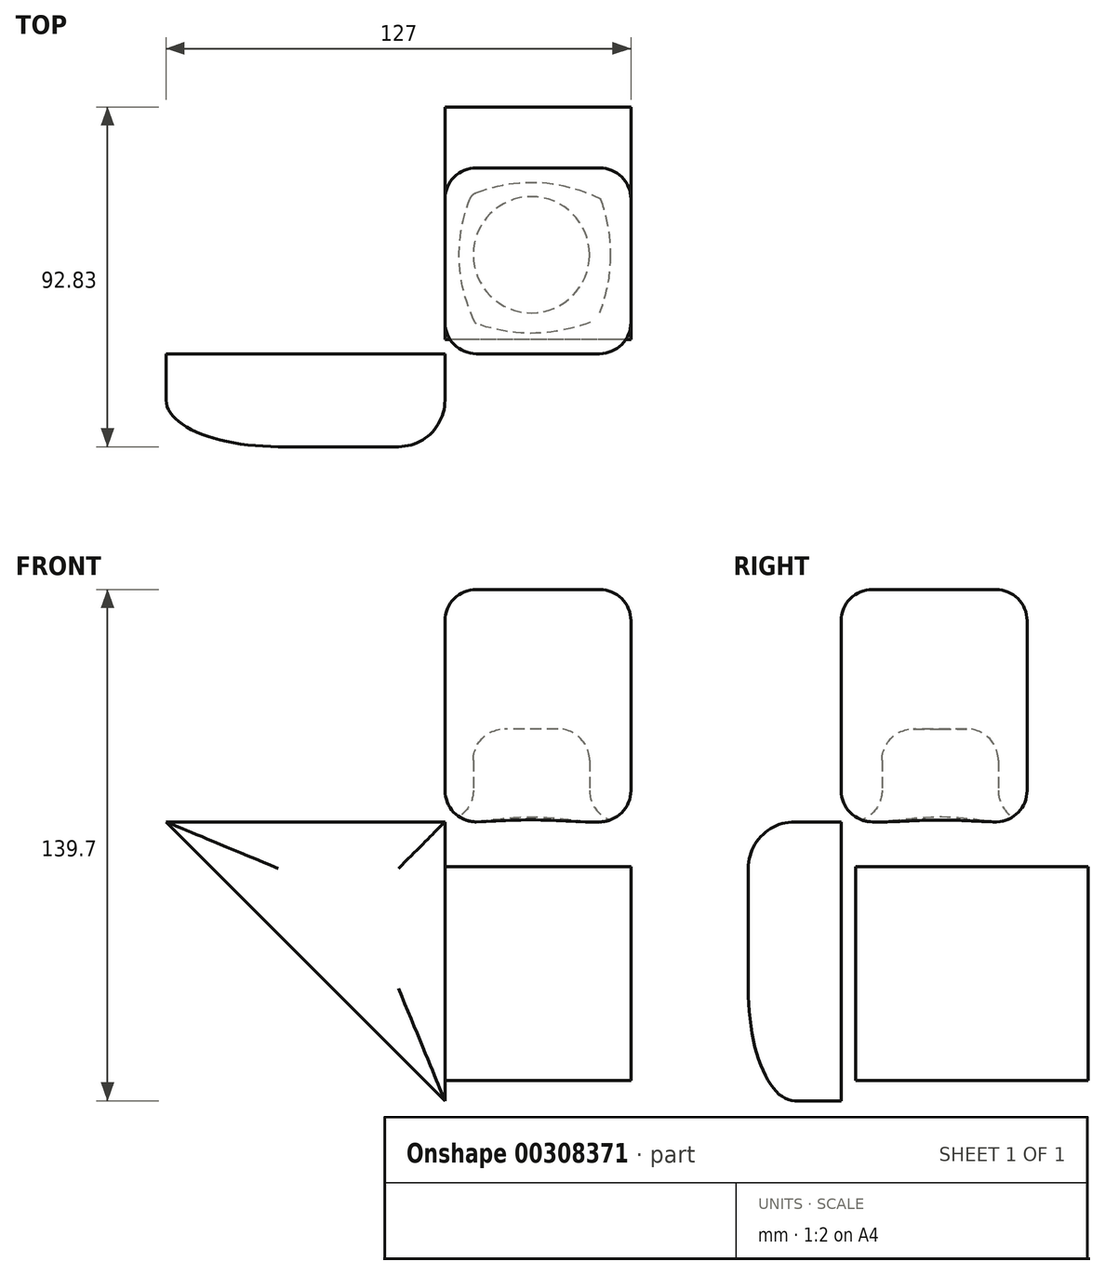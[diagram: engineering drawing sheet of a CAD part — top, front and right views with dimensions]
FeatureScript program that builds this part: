
annotation { "Feature Type Name" : "Feature", "Feature Type Description" : "" }
export const myFeature = defineFeature(function(context is Context, id is Id, definition is map)
    precondition{}
    {
        {
            var Q0;
            Q0=qCreatedBy(makeId("Top.planeOp"),FACE);
            var sketch = newSketch(context, id + "F0", { "sketchPlane" : qUnion([Q0])});
            skLineSegment(sketch, "E0", {"start": v(0, 0) * mm, "end": v(50.8, 0) * mm});
            skLineSegment(sketch, "E1", {"start": v(0, 0) * mm, "end": v(0, 50.8) * mm});
            skLineSegment(sketch, "E2", {"start": v(0, 50.8) * mm, "end": v(50.8, 50.8) * mm});
            skLineSegment(sketch, "E3", {"start": v(50.8, 50.8) * mm, "end": v(50.8, 0) * mm});
            skSolve(sketch);
        }
        {
            var Q0;
            Q0 = qSketchRegion(id + "F0", true);
            extrude(context, id + "F1", {"entities" : qUnion([Q0]), "depth" : 63.5 * mm});
        }
        {
            var Q0;
            Q0=qCreatedBy(makeId("Top.planeOp"),FACE);
            var sketch = newSketch(context, id + "F2", { "sketchPlane" : qUnion([Q0])});
            skCircle(sketch, "E4", {"center": v(23.6, 27.04) * mm, "radius": 15.88 * mm});
            skSolve(sketch);
        }
        {
            var Q0;
            Q0=makeQuery(id+"F2.imprint","IMPRINT",FACE,{"disambiguationData":[TD([[makeQuery(id+"F2.imprint","IMPRINT",EDGE,{"derivedFrom":sQuery(id+"F2.wireOp",EDGE,"E4")}),1.0]])]});
            var Q1;
            Q1=sQuery(id+"F2.wireOp",EDGE,"E4");
            extrude(context, id + "F3", {"entities" : qUnion([Q0]), "surfaceEntities" : qUnion([Q1]), "depth" : 25.4 * mm});
        }
        {
            var Q0;
            Q0=makeQuery(id+"F3.opExtrude","SWEPT_BODY",BODY,{"disambiguationData":[OSD([sQuery(id+"F2.wireOp",EDGE,"E4")])]});
            var Q1;
            Q1=makeQuery(id+"F1.opExtrude","SWEPT_BODY",BODY,{"disambiguationData":[OSD([sQuery(id+"F0.wireOp",EDGE,"E0"),sQuery(id+"F0.wireOp",EDGE,"E1"),sQuery(id+"F0.wireOp",EDGE,"E2"),sQuery(id+"F0.wireOp",EDGE,"E3")])]});
            booleanBodies(context, id + "F4", {"operationType" : BooleanOperationType.SUBTRACTION, "tools" : qUnion([Q0]), "targets" : qUnion([Q1])});
        }
        {
            var Q0;
            Q0=makeQuery(id+"F1.opExtrude","SWEPT_FACE",FACE,{"disambiguationData":[OSD([sQuery(id+"F0.wireOp",EDGE,"E1")])]});
            var Q1;
            Q1=makeQuery(id+"F1.opExtrude","SWEPT_FACE",FACE,{"disambiguationData":[OSD([sQuery(id+"F0.wireOp",EDGE,"E2")])]});
            var Q2;
            Q2=makeQuery(id+"F1.opExtrude","SWEPT_FACE",FACE,{"disambiguationData":[OSD([sQuery(id+"F0.wireOp",EDGE,"E0")])]});
            var Q3;
            Q3=makeQuery(id+"F1.opExtrude","SWEPT_FACE",FACE,{"disambiguationData":[OSD([sQuery(id+"F0.wireOp",EDGE,"E3")])]});
            var Q4;
            Q4=makeQuery(id+"F1.opExtrude","CAP_FACE",FACE,{"disambiguationData":[OSD([sQuery(id+"F0.wireOp",EDGE,"E0"),sQuery(id+"F0.wireOp",EDGE,"E1"),sQuery(id+"F0.wireOp",EDGE,"E2"),sQuery(id+"F0.wireOp",EDGE,"E3")])],"isStart":true});
            var Q5;
            Q5=makeQuery(id+"F4.opBoolean","COPY",FACE,{"derivedFrom":makeQuery(id+"F3.opExtrude","CAP_FACE",FACE,{"disambiguationData":[OSD([sQuery(id+"F2.wireOp",EDGE,"E4")])],"isStart":false})});
            fillet(context, id + "F5", {"entities" : qUnion([Q0, Q1, Q2, Q3, Q4, Q5]), "radius" : 8.58 * mm, "tangentPropagation" : true, "allowEdgeOverflow" : false});
        }
        {
            var Q0;
            Q0=qCreatedBy(makeId("Front.planeOp"),FACE);
            var sketch = newSketch(context, id + "F6", { "sketchPlane" : qUnion([Q0])});
            skLineSegment(sketch, "E5", {"start": v(0, 0) * mm, "end": v(0, -76.2) * mm});
            skLineSegment(sketch, "E6", {"start": v(0, 0) * mm, "end": v(-76.2, 0) * mm});
            skLineSegment(sketch, "E7", {"start": v(-76.2, 0) * mm, "end": v(0, -76.2) * mm});
            skSolve(sketch);
        }
        {
            var Q0;
            Q0=makeQuery(id+"F6.imprint","IMPRINT",FACE,{"disambiguationData":[TD([[makeQuery(id+"F6.imprint","IMPRINT",EDGE,{"derivedFrom":sQuery(id+"F6.wireOp",EDGE,"E5")}),-1.0]])]});
            extrude(context, id + "F7", {"entities" : qUnion([Q0]), "depth" : 25.4 * mm});
        }
        {
            var Q0;
            Q0=makeQuery(id+"F7.opExtrude","CAP_FACE",FACE,{"disambiguationData":[OSD([sQuery(id+"F6.wireOp",EDGE,"E5"),sQuery(id+"F6.wireOp",EDGE,"E6"),sQuery(id+"F6.wireOp",EDGE,"E7")])],"isStart":false});
            fillet(context, id + "F8", {"entities" : qUnion([Q0]), "radius" : 12.7 * mm, "tangentPropagation" : true, "allowEdgeOverflow" : false});
        }
        {
            var Q0;
            Q0=qCreatedBy(makeId("Right.planeOp"),FACE);
            var sketch = newSketch(context, id + "F9", { "sketchPlane" : qUnion([Q0])});
            skLineSegment(sketch, "E8.bottom", {"start": v(3.93, -12.26) * mm, "end": v(67.43, -12.26) * mm});
            skLineSegment(sketch, "E8.top", {"start": v(3.93, -70.68) * mm, "end": v(67.43, -70.68) * mm});
            skLineSegment(sketch, "E8.left", {"start": v(3.93, -12.26) * mm, "end": v(3.93, -70.68) * mm});
            skLineSegment(sketch, "E8.right", {"start": v(67.43, -12.26) * mm, "end": v(67.43, -70.68) * mm});
            skSolve(sketch);
        }
        {
            var Q0;
            Q0=makeQuery(id+"F9.imprint","IMPRINT",FACE,{"disambiguationData":[TD([[makeQuery(id+"F9.imprint","IMPRINT",EDGE,{"derivedFrom":sQuery(id+"F9.wireOp",EDGE,"E8.bottom")}),-1.0]])]});
            extrude(context, id + "F10", {"entities" : qUnion([Q0]), "depth" : 50.8 * mm});
        }
    });
